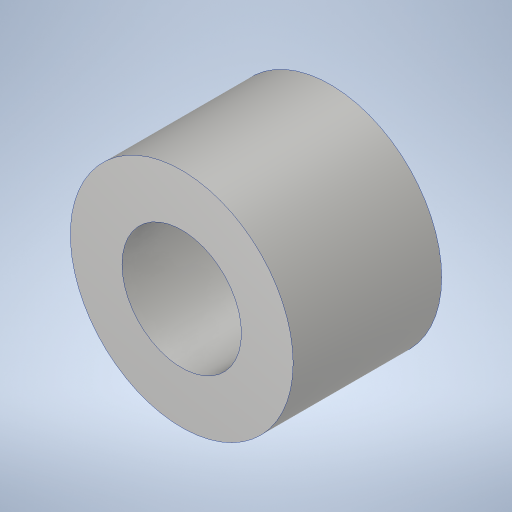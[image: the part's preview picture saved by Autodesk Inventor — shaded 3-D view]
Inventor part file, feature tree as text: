
AUTODESK INVENTOR PART (.ipt)
format: ipt  version: 2023.3 (Build 273359000, 359)  size: 226,304 bytes
history: native  units: in
note: dims shown in document units (in); Inventor stores cm internally (conversion verified against a paired STEP export)
features: sketch x1, extrude x1, hole x1
ambient origin geometry x8: Origin, YZ Plane, XZ Plane, XY Plane, X Axis, Y Axis, Z Axis, Center Point
bodies: Solid1 (feature_tree)
feature tree (3):
  sketch  "Sketch1"  dims[d1=0.25in d2=0.0in d3=0.201in d4=0.75in d5=0.385in d6=0.25in d7=0.5635in d8=1.0in d9=0.8108in d10=0.375in]
  extrude  "Extrusion1"  TaperAngle=0.0deg  [1 undecoded]
  hole  "Hole1"  [1 undecoded]
note: 2 required parameter values undecoded (feature->parameter linkage not recoverable at this tier; creation-order binding heuristic only, values carry confidence <= 0.55)
